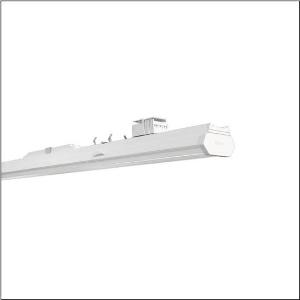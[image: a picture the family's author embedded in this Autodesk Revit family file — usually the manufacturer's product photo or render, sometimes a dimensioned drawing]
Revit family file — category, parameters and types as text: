
# Revit family: licross_r__11_protected_mo_51tp12dn495g3s4_346c
name_source: partatom
category: Lighting Fixtures
units: mm (PartAtom-declared; Revit-internal decimal feet)

## family parameters
Cut with Voids When Loaded = No
Host = Face
Light Source = No
Part Type = Normal
Room Calculation Point = No
Round Connector Dimension = Use Diameter
Shared = No

## types (1)
- --- (1 x LED, 980 lm, 6.8 W, 4000K)
    Apparent Load = 7 VA
    CIE Flux Codes = 73 92 98 99 100
    Color Rendering = 80
    Color Temperature = 4000K
    Default Elevation = 1800 mm
    Description = Licross® 11 Protected MO, luminaire insert, of sheet steel, galvanised, coil coated, white, length: 1.500mm, width: 90mm, height: 101mm, LED rated luminous flux: 9.980lm, light colour: 840, control gear: DALI 2, with plug, 6-pole, with phase selection, for trunking rail, 9 or 11-core, mains connection: 220..240V, AC, 50/60Hz, rated input power: 61W, for trunking rail, 9-/11-core, halogen-free wiring, for emergency light function, converter,control gear: single battery element, battery: LiFeP04, 9Ah, primary light control with lens, of plastic, primary optical cover: cover, of PMMA, light emission: direct distribution, primary light characteristic: symmetric, protection rating (complete): IP64, insulation class (complete): insulation class I (protective earthing), certification: CE, UKCA, protection symbol: D if used in an environment with conductive dust loads with corresponding accessories, impact resistance: IK06, permissible ambient temperature for indoor applications: +5..+35°C, standard: EN 60598-2-22, LABS conformity tested according to VDMA 24364:2018-05, reducing of maximum allowable ambient temperature of 5°C with ceiling mounting, corresponds to IFS (International Featured Standards) requirements for safety and quality in the food industry, packaging unit: 1 piece
    Height = 92 mm
    Lamp = 1 x LED
    Lamp Light Flux = 980 lm
    Lamp Power = 6.8 W
    Lamp count = 1
    Length = 1500 mm
    Luminous efficacy = 144 lm/W
    Manufacturer = Siteco
    ModVariant = No
    Model = 51TP12DN495G3S4
    Mounting Place = Ceiling
    Mounting Type = Pendant
    Number of Poles = 1
    OnlyDefault = Yes
    Power Factor = 1
    Product Name = Licross® 11 Protected MO
    Product group = luminaire insert
    ProductGroupID = 901
    Protection Class = Protection class I
    Protection Degree = IP 64
    RLX_Detail_Level = 1
    RLX_Emergency_Light_Flux = 0 lm
    RLX_Emergency_Type = 0
    RLX_Emergency_Type_DB = No
    RlxData = <blob elided: 24677 chars, md5=b2e016d7>
    Socket = socket
    Standby Power = 0 W
    System Light Flux = 980 lm
    System Power = 7 W
    Type Comments = : emergency light operation: 3 h
    Type Image = l_1256148.jpg
    URL = http://relux.com
    VarID = @adj_041127
    Voltage = 0 V
    Weight = 0.00 kg
    Width = 88 mm

## geometry (parser evidence)
native form markers: Blend x4, Sweep x10
no freeform markers — native parametric forms only
